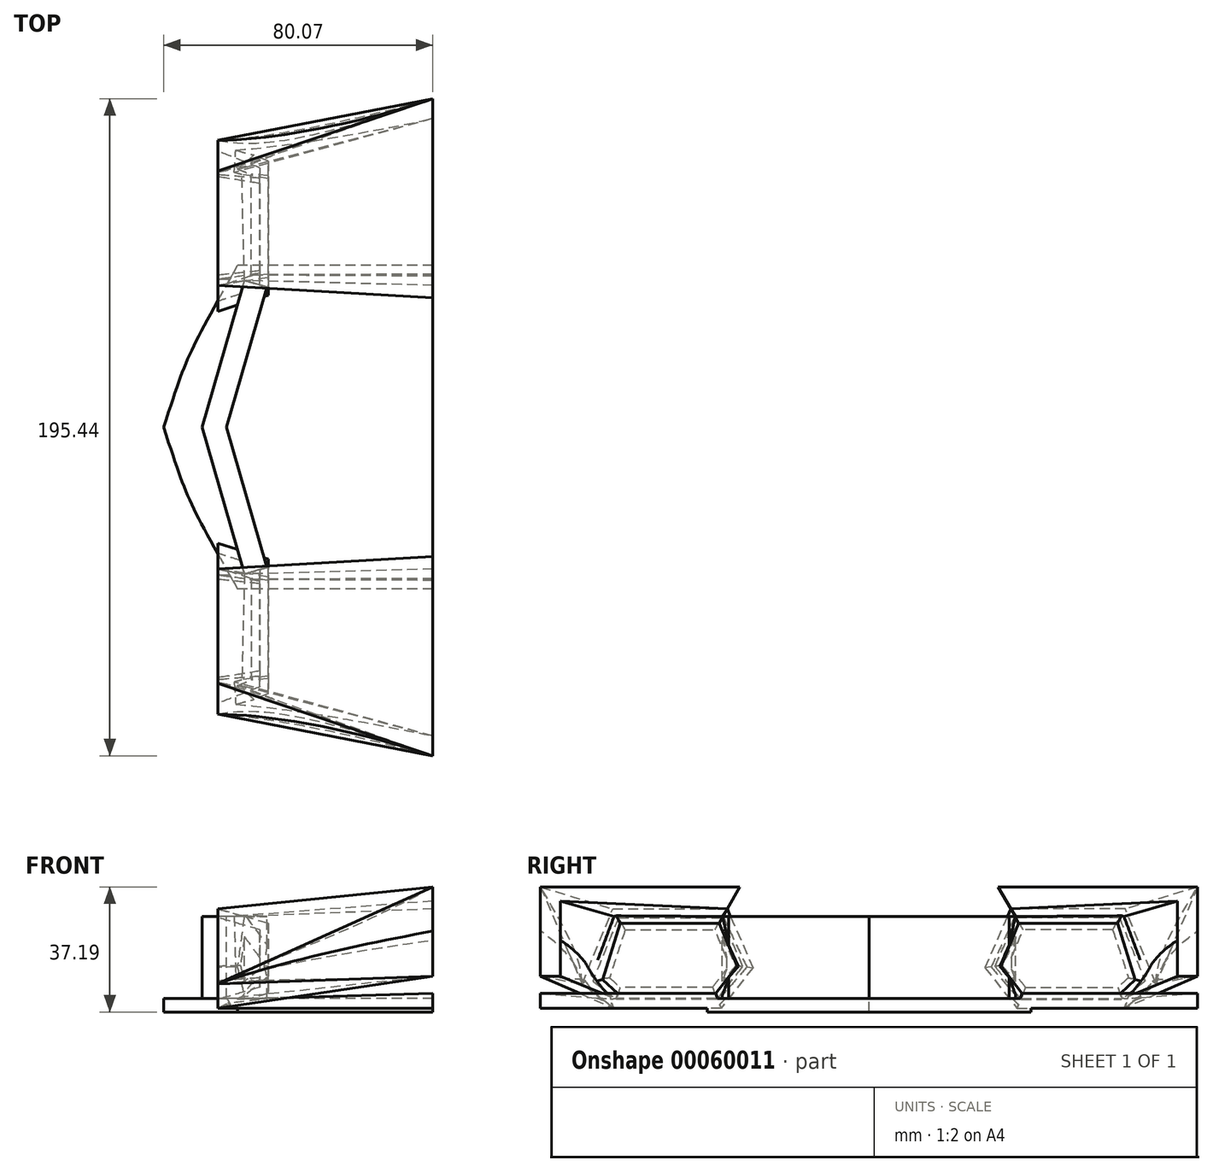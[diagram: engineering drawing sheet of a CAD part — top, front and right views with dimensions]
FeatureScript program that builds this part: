
annotation { "Feature Type Name" : "Feature", "Feature Type Description" : "" }
export const myFeature = defineFeature(function(context is Context, id is Id, definition is map)
    precondition{}
    {
        {
            var Q0;
            Q0=qCreatedBy(makeId("Top.planeOp"),FACE);
            var sketch = newSketch(context, id + "F0", { "sketchPlane" : qUnion([Q0])});
            skPoint(sketch, "E0", {"position": v(-74.63, 89.12) * mm});
            skPoint(sketch, "E1", {"position": v(-74.63, 0) * mm});
            skPoint(sketch, "E2", {"position": v(-156.71, 98.72) * mm});
            skPoint(sketch, "E3", {"position": v(-156.71, 88.06) * mm});
            skSolve(sketch);
        }
        {
            var Q0;
            Q0=qCreatedBy(makeId("Front.planeOp"),FACE);
            var sketch = newSketch(context, id + "F1", { "sketchPlane" : qUnion([Q0])});
            skPoint(sketch, "E4.0", {"position": v(-239, 0) * mm});
            skPoint(sketch, "E5.0", {"position": v(239, 0) * mm});
            skPoint(sketch, "E6", {"position": v(-86.17, 65.26) * mm});
            skSolve(sketch);
        }
        {
            var Q0;
            Q0=qCreatedBy(makeId("Right.planeOp"),FACE);
            cPlane(context, id + "F2", {"entities" : qUnion([Q0]), "cplaneType" : CPlaneType.OFFSET, "offset" : 218.37 * mm, "oppositeDirection" : true, "width" : 150 * mm, "height" : 150 * mm});
        }
        {
            var Q0;
            Q0=qCreatedBy(id+"F2.planeOp",FACE);
            var sketch = newSketch(context, id + "F3", { "sketchPlane" : qUnion([Q0])});
            skPoint(sketch, "E7", {"position": v(76.2, 48.85) * mm});
            skLineSegment(sketch, "E8", {"start": v(76.2, 48.85) * mm, "end": v(42.19, 48.85) * mm});
            skLineSegment(sketch, "E9", {"start": v(42.19, 48.85) * mm, "end": v(34.5, 31.38) * mm});
            skLineSegment(sketch, "E10", {"start": v(34.5, 31.38) * mm, "end": v(44, 19.32) * mm});
            skLineSegment(sketch, "E11", {"start": v(44, 19.32) * mm, "end": v(75.98, 19.32) * mm});
            skLineSegment(sketch, "E12", {"start": v(75.98, 19.32) * mm, "end": v(85.33, 26.56) * mm});
            skLineSegment(sketch, "E13", {"start": v(85.33, 26.56) * mm, "end": v(76.2, 48.85) * mm});
            skSolve(sketch);
        }
        {
            var Q0;
            Q0=qCreatedBy(id+"F2.planeOp",FACE);
            cPlane(context, id + "F4", {"entities" : qUnion([Q0]), "cplaneType" : CPlaneType.OFFSET, "offset" : 15 * mm, "width" : 150 * mm, "height" : 150 * mm});
        }
        {
            var Q0;
            Q0=qCreatedBy(id+"F4.planeOp",FACE);
            var sketch = newSketch(context, id + "F5", { "sketchPlane" : qUnion([Q0])});
            skLineSegment(sketch, "E14", {"start": v(73.97, 44.52) * mm, "end": v(44.5, 44.52) * mm});
            skLineSegment(sketch, "E15", {"start": v(44.5, 44.52) * mm, "end": v(39.26, 31.82) * mm});
            skLineSegment(sketch, "E16", {"start": v(39.26, 31.82) * mm, "end": v(45.52, 23.7) * mm});
            skLineSegment(sketch, "E17", {"start": v(45.52, 23.7) * mm, "end": v(74.81, 23.7) * mm});
            skLineSegment(sketch, "E18", {"start": v(74.81, 23.7) * mm, "end": v(79.22, 27.75) * mm});
            skLineSegment(sketch, "E19", {"start": v(79.22, 27.75) * mm, "end": v(73.97, 44.52) * mm});
            skSolve(sketch);
        }
        {
            var Q0;
            Q0=makeQuery(id+"F5.imprint","IMPRINT",FACE,{"disambiguationData":[TD([[makeQuery(id+"F5.imprint","IMPRINT",EDGE,{"derivedFrom":sQuery(id+"F5.wireOp",EDGE,"E14")}),1.0]])]});
            var Q1;
            Q1=makeQuery(id+"F3.imprint","IMPRINT",FACE,{"disambiguationData":[TD([[makeQuery(id+"F3.imprint","IMPRINT",EDGE,{"derivedFrom":sQuery(id+"F3.wireOp",EDGE,"E8")}),1.0]])]});
            loft(context, id + "F6", {"sheetProfilesArray" : [{ "sheetProfileEntities" : qUnion([Q0]) }, { "sheetProfileEntities" : qUnion([Q1]) }]});
        }
        {
            var Q0;
            Q0=makeQuery(id+"F6.opLoft","CAP_FACE",FACE,{"disambiguationData":[OSD([makeQuery(id+"F3.imprint","IMPRINT",FACE,{"disambiguationData":[TD([[makeQuery(id+"F3.imprint","IMPRINT",EDGE,{"derivedFrom":sQuery(id+"F3.wireOp",EDGE,"E8")}),1.0]])]})])],"isStart":true});
            shell(context, id + "F7", {"entities" : qUnion([Q0]), "thickness" : 2.5 * mm});
        }
        {
            var Q0;
            Q0=makeQuery(id+"F6.opLoft","CAP_FACE",FACE,{"disambiguationData":[OSD([makeQuery(id+"F3.imprint","IMPRINT",FACE,{"disambiguationData":[TD([[makeQuery(id+"F3.imprint","IMPRINT",EDGE,{"derivedFrom":sQuery(id+"F3.wireOp",EDGE,"E8")}),1.0]])]})])],"isStart":true});
            var sketch = newSketch(context, id + "F8", { "sketchPlane" : qUnion([Q0])});
            skPoint(sketch, "E20.0", {"position": v(-76.2, 48.85) * mm});
            skPoint(sketch, "E21.0", {"position": v(-74.49, 46.25) * mm});
            skPoint(sketch, "E22.0", {"position": v(-82.13, 27.4) * mm});
            skPoint(sketch, "E23.0", {"position": v(-85.33, 26.56) * mm});
            skLineSegment(sketch, "E24", {"start": v(-85.33, 26.56) * mm, "end": v(-76.2, 48.85) * mm});
            skLineSegment(sketch, "E25", {"start": v(-85.33, 26.56) * mm, "end": v(-82.13, 27.4) * mm});
            skLineSegment(sketch, "E26", {"start": v(-82.13, 27.4) * mm, "end": v(-74.49, 46.25) * mm});
            skLineSegment(sketch, "E27", {"start": v(-74.49, 46.25) * mm, "end": v(-76.2, 48.85) * mm});
            skSolve(sketch);
        }
        {
            var Q0;
            Q0=qCreatedBy(makeId("Front.planeOp"),FACE);
            var sketch = newSketch(context, id + "F9", { "sketchPlane" : qUnion([Q0])});
            skPoint(sketch, "E28", {"position": v(-154.45, 57.19) * mm});
            skSolve(sketch);
        }
        {
            var Q0;
            Q0=qCreatedBy(makeId("Right.planeOp"),FACE);
            var Q1;
            Q1=sQuery(id+"F9.wireOp",VERTEX,"E28");
            cPlane(context, id + "F10", {"entities" : qUnion([Q0, Q1]), "cplaneType" : CPlaneType.PLANE_POINT, "offset" : 150 * mm, "width" : 150 * mm, "height" : 150 * mm});
        }
        {
            var Q0;
            Q0=qCreatedBy(id+"F10.planeOp",FACE);
            var sketch = newSketch(context, id + "F11", { "sketchPlane" : qUnion([Q0])});
            skPoint(sketch, "E29", {"position": v(97.72, 55.38) * mm});
            skLineSegment(sketch, "E30", {"start": v(97.72, 55.38) * mm, "end": v(97.72, 28.82) * mm});
            skLineSegment(sketch, "E31", {"start": v(97.72, 28.82) * mm, "end": v(91.8, 28.82) * mm});
            skLineSegment(sketch, "E32", {"start": v(91.8, 28.82) * mm, "end": v(91.8, 51.17) * mm});
            skLineSegment(sketch, "E33", {"start": v(91.8, 51.17) * mm, "end": v(97.72, 55.38) * mm});
            skSolve(sketch);
        }
        {
            var Q1;
            Q1=makeQuery(id+"F11.imprint","IMPRINT",FACE,{"disambiguationData":[TD([[makeQuery(id+"F11.imprint","IMPRINT",EDGE,{"derivedFrom":sQuery(id+"F11.wireOp",EDGE,"E30")}),-1.0]])]});
            var Q2;
            Q2=makeQuery(id+"F8.imprint","IMPRINT",FACE,{"disambiguationData":[TD([[makeQuery(id+"F8.imprint","IMPRINT",EDGE,{"derivedFrom":sQuery(id+"F8.wireOp",EDGE,"E24")}),1.0]])]});
            loft(context, id + "F12", {"operationType" : NewBodyOperationType.ADD, "sheetProfilesArray" : [{ "sheetProfileEntities" : qUnion([Q1]) }, { "sheetProfileEntities" : qUnion([Q2]) }]});
        }
        {
            var Q0;
            Q0=makeQuery(id+"F6.opLoft","CAP_FACE",FACE,{"disambiguationData":[OSD([makeQuery(id+"F3.imprint","IMPRINT",FACE,{"disambiguationData":[TD([[makeQuery(id+"F3.imprint","IMPRINT",EDGE,{"derivedFrom":sQuery(id+"F3.wireOp",EDGE,"E8")}),1.0]])]})])],"isStart":true});
            var sketch = newSketch(context, id + "F13", { "sketchPlane" : qUnion([Q0])});
            skPoint(sketch, "E34.0", {"position": v(-85.33, 26.56) * mm});
            skPoint(sketch, "E35.0", {"position": v(-82.13, 27.4) * mm});
            skPoint(sketch, "E36.0", {"position": v(-75.1, 21.92) * mm});
            skPoint(sketch, "E37.0", {"position": v(-75.98, 19.32) * mm});
            skLineSegment(sketch, "E38", {"start": v(-85.33, 26.56) * mm, "end": v(-82.13, 27.4) * mm});
            skLineSegment(sketch, "E39", {"start": v(-82.13, 27.4) * mm, "end": v(-75.1, 21.92) * mm});
            skLineSegment(sketch, "E40", {"start": v(-75.1, 21.92) * mm, "end": v(-75.98, 19.32) * mm});
            skLineSegment(sketch, "E41", {"start": v(-75.98, 19.32) * mm, "end": v(-85.33, 26.56) * mm});
            skSolve(sketch);
        }
        {
            var Q0;
            Q0=makeQuery(id+"F12.opLoft","CAP_FACE",FACE,{"disambiguationData":[OSD([makeQuery(id+"F11.imprint","IMPRINT",FACE,{"disambiguationData":[TD([[makeQuery(id+"F11.imprint","IMPRINT",EDGE,{"derivedFrom":sQuery(id+"F11.wireOp",EDGE,"E30")}),-1.0]])]})])],"isStart":true});
            var sketch = newSketch(context, id + "F14", { "sketchPlane" : qUnion([Q0])});
            skFitSpline(sketch, "E42.0", {"points": [v(97.72, 28.82) * mm, v(95.75, 28.82) * mm, v(93.77, 28.82) * mm, v(91.8, 28.82) * mm]});
            skPoint(sketch, "E43.0", {"position": v(75.98, 19.32) * mm});
            skLineSegment(sketch, "E44", {"start": v(91.8, 28.82) * mm, "end": v(91.8, 19.32) * mm});
            skLineSegment(sketch, "E45", {"start": v(91.8, 19.32) * mm, "end": v(97.72, 19.32) * mm});
            skLineSegment(sketch, "E46", {"start": v(97.72, 19.32) * mm, "end": v(97.72, 28.82) * mm});
            skSolve(sketch);
        }
        {
            var Q1;
            Q1=makeQuery(id+"F14.imprint","IMPRINT",FACE,{"disambiguationData":[TD([[makeQuery(id+"F14.imprint","IMPRINT",EDGE,{"derivedFrom":sQuery(id+"F14.wireOp",EDGE,"E42.0")}),-1.0]])]});
            var Q2;
            Q2=makeQuery(id+"F13.imprint","IMPRINT",FACE,{"disambiguationData":[TD([[makeQuery(id+"F13.imprint","IMPRINT",EDGE,{"derivedFrom":sQuery(id+"F13.wireOp",EDGE,"E38")}),-1.0]])]});
            loft(context, id + "F15", {"operationType" : NewBodyOperationType.ADD, "sheetProfilesArray" : [{ "sheetProfileEntities" : qUnion([Q1]) }, { "sheetProfileEntities" : qUnion([Q2]) }]});
        }
        {
            var Q0;
            Q0=makeQuery(id+"F6.opLoft","CAP_FACE",FACE,{"disambiguationData":[OSD([makeQuery(id+"F3.imprint","IMPRINT",FACE,{"disambiguationData":[TD([[makeQuery(id+"F3.imprint","IMPRINT",EDGE,{"derivedFrom":sQuery(id+"F3.wireOp",EDGE,"E8")}),1.0]])]})])],"isStart":true});
            var sketch = newSketch(context, id + "F16", { "sketchPlane" : qUnion([Q0])});
            skPoint(sketch, "E47.0", {"position": v(-76.2, 48.85) * mm});
            skPoint(sketch, "E48.0", {"position": v(-74.49, 46.25) * mm});
            skPoint(sketch, "E49.0", {"position": v(-43.87, 46.25) * mm});
            skPoint(sketch, "E50.0", {"position": v(-42.19, 48.85) * mm});
            skLineSegment(sketch, "E51", {"start": v(-76.2, 48.85) * mm, "end": v(-74.49, 46.25) * mm});
            skLineSegment(sketch, "E52", {"start": v(-76.2, 48.85) * mm, "end": v(-42.19, 48.85) * mm});
            skLineSegment(sketch, "E53", {"start": v(-42.19, 48.85) * mm, "end": v(-43.87, 46.25) * mm});
            skLineSegment(sketch, "E54", {"start": v(-43.87, 46.25) * mm, "end": v(-74.49, 46.25) * mm});
            skSolve(sketch);
        }
        {
            var Q0;
            Q0=makeQuery(id+"F15.boolean.opBoolean","MERGE",FACE,{"derivedFrom":[makeQuery(id+"F12.opLoft","CAP_FACE",FACE,{"disambiguationData":[OSD([makeQuery(id+"F11.imprint","IMPRINT",FACE,{"disambiguationData":[TD([[makeQuery(id+"F11.imprint","IMPRINT",EDGE,{"derivedFrom":sQuery(id+"F11.wireOp",EDGE,"E30")}),-1.0]])]})])],"isStart":true}),makeQuery(id+"F15.opLoft","CAP_FACE",FACE,{"disambiguationData":[OSD([makeQuery(id+"F14.imprint","IMPRINT",FACE,{"disambiguationData":[TD([[makeQuery(id+"F14.imprint","IMPRINT",EDGE,{"derivedFrom":sQuery(id+"F14.wireOp",EDGE,"E42.0")}),-1.0]])]})])],"isStart":true})]});
            var sketch = newSketch(context, id + "F17", { "sketchPlane" : qUnion([Q0])});
            skPoint(sketch, "E55.0", {"position": v(97.72, 55.38) * mm});
            skPoint(sketch, "E56.0", {"position": v(42.19, 48.85) * mm});
            skLineSegment(sketch, "E57", {"start": v(97.72, 55.38) * mm, "end": v(38.45, 55.38) * mm});
            skFitSpline(sketch, "E58.0", {"points": [v(91.8, 51.17) * mm, v(93.77, 52.57) * mm, v(95.75, 53.97) * mm, v(97.72, 55.38) * mm]});
            skLineSegment(sketch, "E59", {"start": v(38.45, 55.38) * mm, "end": v(42.19, 48.85) * mm});
            skLineSegment(sketch, "E60", {"start": v(42.19, 48.85) * mm, "end": v(91.8, 51.17) * mm});
            skSolve(sketch);
        }
        {
            var Q1;
            Q1=makeQuery(id+"F17.imprint","IMPRINT",FACE,{"disambiguationData":[TD([[makeQuery(id+"F17.imprint","IMPRINT",EDGE,{"derivedFrom":sQuery(id+"F17.wireOp",EDGE,"E57")}),1.0]])]});
            var Q2;
            Q2=makeQuery(id+"F16.imprint","IMPRINT",FACE,{"disambiguationData":[TD([[makeQuery(id+"F16.imprint","IMPRINT",EDGE,{"derivedFrom":sQuery(id+"F16.wireOp",EDGE,"E51")}),1.0]])]});
            loft(context, id + "F18", {"operationType" : NewBodyOperationType.ADD, "sheetProfilesArray" : [{ "sheetProfileEntities" : qUnion([Q1]) }, { "sheetProfileEntities" : qUnion([Q2]) }]});
        }
        {
            var Q0;
            Q0=makeQuery(id+"F6.opLoft","CAP_FACE",FACE,{"disambiguationData":[OSD([makeQuery(id+"F3.imprint","IMPRINT",FACE,{"disambiguationData":[TD([[makeQuery(id+"F3.imprint","IMPRINT",EDGE,{"derivedFrom":sQuery(id+"F3.wireOp",EDGE,"E8")}),1.0]])]})])],"isStart":true});
            var sketch = newSketch(context, id + "F19", { "sketchPlane" : qUnion([Q0])});
            skPoint(sketch, "E61.0", {"position": v(-75.98, 19.32) * mm});
            skPoint(sketch, "E62.0", {"position": v(-75.1, 21.92) * mm});
            skPoint(sketch, "E63.0", {"position": v(-45.24, 21.92) * mm});
            skPoint(sketch, "E64.0", {"position": v(-44, 19.32) * mm});
            skLineSegment(sketch, "E65", {"start": v(-75.98, 19.32) * mm, "end": v(-44, 19.32) * mm});
            skLineSegment(sketch, "E66", {"start": v(-44, 19.32) * mm, "end": v(-45.24, 21.92) * mm});
            skLineSegment(sketch, "E67", {"start": v(-45.24, 21.92) * mm, "end": v(-75.1, 21.92) * mm});
            skLineSegment(sketch, "E68", {"start": v(-75.1, 21.92) * mm, "end": v(-75.98, 19.32) * mm});
            skSolve(sketch);
        }
        {
            var Q0;
            Q0=makeQuery(id+"F18.boolean.opBoolean","MERGE",FACE,{"derivedFrom":[makeQuery(id+"F15.boolean.opBoolean","MERGE",FACE,{"derivedFrom":[makeQuery(id+"F12.opLoft","CAP_FACE",FACE,{"disambiguationData":[OSD([makeQuery(id+"F11.imprint","IMPRINT",FACE,{"disambiguationData":[TD([[makeQuery(id+"F11.imprint","IMPRINT",EDGE,{"derivedFrom":sQuery(id+"F11.wireOp",EDGE,"E30")}),-1.0]])]})])],"isStart":true}),makeQuery(id+"F15.opLoft","CAP_FACE",FACE,{"disambiguationData":[OSD([makeQuery(id+"F14.imprint","IMPRINT",FACE,{"disambiguationData":[TD([[makeQuery(id+"F14.imprint","IMPRINT",EDGE,{"derivedFrom":sQuery(id+"F14.wireOp",EDGE,"E42.0")}),-1.0]])]})])],"isStart":true})]}),makeQuery(id+"F18.opLoft","CAP_FACE",FACE,{"disambiguationData":[OSD([makeQuery(id+"F17.imprint","IMPRINT",FACE,{"disambiguationData":[TD([[makeQuery(id+"F17.imprint","IMPRINT",EDGE,{"derivedFrom":sQuery(id+"F17.wireOp",EDGE,"E57")}),1.0]])]})])],"isStart":true})]});
            cPlane(context, id + "F20", {"entities" : qUnion([Q0]), "cplaneType" : CPlaneType.OFFSET, "offset" : 0 * mm, "width" : 150 * mm, "height" : 150 * mm});
        }
        {
            var Q0;
            Q0=qCreatedBy(id+"F20.planeOp",FACE);
            var sketch = newSketch(context, id + "F21", { "sketchPlane" : qUnion([Q0])});
            skPoint(sketch, "E69.0", {"position": v(97.72, 19.32) * mm});
            skPoint(sketch, "E70.0", {"position": v(45.52, 23.7) * mm});
            skPoint(sketch, "E71.0", {"position": v(44, 19.32) * mm});
            skLineSegment(sketch, "E72", {"start": v(44, 19.32) * mm, "end": v(97.72, 19.32) * mm});
            skLineSegment(sketch, "E73", {"start": v(45.52, 23.7) * mm, "end": v(44, 19.32) * mm});
            skLineSegment(sketch, "E74", {"start": v(45.52, 23.7) * mm, "end": v(97.72, 23.7) * mm});
            skLineSegment(sketch, "E75", {"start": v(97.72, 23.7) * mm, "end": v(97.72, 19.32) * mm});
            skSolve(sketch);
        }
        {
            var Q1;
            Q1=makeQuery(id+"F21.imprint","IMPRINT",FACE,{"disambiguationData":[TD([[makeQuery(id+"F21.imprint","IMPRINT",EDGE,{"derivedFrom":sQuery(id+"F21.wireOp",EDGE,"E72")}),1.0]])]});
            var Q2;
            Q2=makeQuery(id+"F19.imprint","IMPRINT",FACE,{"disambiguationData":[TD([[makeQuery(id+"F19.imprint","IMPRINT",EDGE,{"derivedFrom":sQuery(id+"F19.wireOp",EDGE,"E65")}),1.0]])]});
            loft(context, id + "F22", {"operationType" : NewBodyOperationType.ADD, "sheetProfilesArray" : [{ "sheetProfileEntities" : qUnion([Q1]) }, { "sheetProfileEntities" : qUnion([Q2]) }]});
        }
        {
            var Q0;
            Q0=qCreatedBy(makeId("Top.planeOp"),FACE);
            var Q1;
            {var subQ0=sQuery(id+"F21.wireOp",EDGE,"E74");var subQ1=sQuery(id+"F21.wireOp",EDGE,"E73");var subQ2=sQuery(id+"F19.wireOp",EDGE,"E67");var subQ3=sQuery(id+"F19.wireOp",EDGE,"E66");var subQ4=sQuery(id+"F3.wireOp",EDGE,"E12");var subQ5=sQuery(id+"F3.wireOp",EDGE,"E11");var subQ6=sQuery(id+"F3.wireOp",EDGE,"E10");var subQ7=sQuery(id+"F3.wireOp",EDGE,"E9");Q1=makeQuery(id+"F22.boolean.opBoolean","INTERSECT",VERTEX,{"derivedFrom":[makeQuery(id+"F6.opLoft","SWEPT_FACE",FACE,{"disambiguationData":[OSD([subQ6,subQ5,subQ4,sQuery(id+"F5.wireOp",EDGE,"E16"),sQuery(id+"F5.wireOp",EDGE,"E17"),sQuery(id+"F5.wireOp",EDGE,"E18")])]}),makeQuery(id+"F22.opLoft","SWEPT_FACE",FACE,{"disambiguationData":[OSD([subQ7,subQ6,subQ5,sQuery(id+"F19.wireOp",EDGE,"E65"),subQ3,subQ2,sQuery(id+"F21.wireOp",EDGE,"E72"),subQ1,subQ0])]}),makeQuery(id+"F22.opLoft","SWEPT_FACE",FACE,{"disambiguationData":[OSD([subQ7,subQ6,subQ5,subQ4,sQuery(id+"F3.wireOp",EDGE,"E13"),subQ3,subQ2,sQuery(id+"F19.wireOp",EDGE,"E68"),subQ1,subQ0,sQuery(id+"F21.wireOp",EDGE,"E75")])]})]});}
            cPlane(context, id + "F23", {"entities" : qUnion([Q0, Q1]), "cplaneType" : CPlaneType.PLANE_POINT, "offset" : 150 * mm, "width" : 150 * mm, "height" : 150 * mm});
        }
        {
            var Q0;
            Q0=qCreatedBy(id+"F23.planeOp",FACE);
            var sketch = newSketch(context, id + "F24", { "sketchPlane" : qUnion([Q0])});
            skLineSegment(sketch, "E76", {"start": v(-154.45, 0) * mm, "end": v(-234.52, 0) * mm});
            skLineSegment(sketch, "E77", {"start": v(-154.45, 0) * mm, "end": v(-154.45, 48.1) * mm});
            skLineSegment(sketch, "E78", {"start": v(-154.45, 48.1) * mm, "end": v(-212.5, 48.1) * mm});
            skFitSpline(sketch, "E79", {"points": [v(-234.52, 0) * mm, v(-212.5, 48.1) * mm], "startDerivative": vector(21.4, 65.5) * mm, "endDerivative": vector(44.68, 78.83) * mm});
            skSolve(sketch);
        }
        {
            var Q0;
            Q0=makeQuery(id+"F24.imprint","IMPRINT",FACE,{"disambiguationData":[TD([[makeQuery(id+"F24.imprint","IMPRINT",EDGE,{"derivedFrom":sQuery(id+"F24.wireOp",EDGE,"E76")}),-1.0]])]});
            extrude(context, id + "F25", {"entities" : qUnion([Q0]), "operationType" : NewBodyOperationType.ADD, "oppositeDirection" : true, "depth" : 4 * mm});
        }
        {
            var Q0;
            Q0=qCreatedBy(id+"F23.planeOp",FACE);
            var Q1;
            {var subQ0=sQuery(id+"F17.wireOp",EDGE,"E60");var subQ1=sQuery(id+"F17.wireOp",EDGE,"E59");var subQ2=sQuery(id+"F16.wireOp",EDGE,"E54");var subQ3=sQuery(id+"F16.wireOp",EDGE,"E53");var subQ4=sQuery(id+"F3.wireOp",EDGE,"E13");var subQ5=sQuery(id+"F3.wireOp",EDGE,"E10");var subQ6=sQuery(id+"F3.wireOp",EDGE,"E9");var subQ7=sQuery(id+"F3.wireOp",EDGE,"E8");Q1=makeQuery(id+"F18.boolean.opBoolean","INTERSECT",VERTEX,{"derivedFrom":[makeQuery(id+"F6.opLoft","SWEPT_FACE",FACE,{"disambiguationData":[OSD([subQ7,subQ6,subQ4,sQuery(id+"F5.wireOp",EDGE,"E14"),sQuery(id+"F5.wireOp",EDGE,"E15"),sQuery(id+"F5.wireOp",EDGE,"E19")])]}),makeQuery(id+"F18.opLoft","SWEPT_FACE",FACE,{"disambiguationData":[OSD([subQ7,subQ6,subQ5,sQuery(id+"F16.wireOp",EDGE,"E52"),subQ3,subQ2,sQuery(id+"F17.wireOp",EDGE,"E57"),subQ1,subQ0])]}),makeQuery(id+"F18.opLoft","SWEPT_FACE",FACE,{"disambiguationData":[OSD([subQ7,subQ6,subQ5,sQuery(id+"F3.wireOp",EDGE,"E12"),subQ4,sQuery(id+"F11.wireOp",EDGE,"E31"),sQuery(id+"F11.wireOp",EDGE,"E32"),sQuery(id+"F11.wireOp",EDGE,"E33"),sQuery(id+"F16.wireOp",EDGE,"E51"),subQ3,subQ2,sQuery(id+"F17.wireOp",EDGE,"E58.0"),subQ1,subQ0])]})]});}
            cPlane(context, id + "F26", {"entities" : qUnion([Q0, Q1]), "cplaneType" : CPlaneType.PLANE_POINT, "offset" : 150 * mm, "width" : 150 * mm, "height" : 150 * mm});
        }
        {
            var Q0;
            Q0=qCreatedBy(id+"F26.planeOp",FACE);
            var sketch = newSketch(context, id + "F27", { "sketchPlane" : qUnion([Q0])});
            skPoint(sketch, "E80.0", {"position": v(-210.48, 43.66) * mm});
            skLineSegment(sketch, "E81", {"start": v(-210.48, 43.66) * mm, "end": v(-223.12, 0) * mm});
            skLineSegment(sketch, "E82", {"start": v(-210.48, 43.66) * mm, "end": v(-203.8, 41.72) * mm});
            skLineSegment(sketch, "E83", {"start": v(-203.8, 41.72) * mm, "end": v(-215.88, 0) * mm});
            skLineSegment(sketch, "E84", {"start": v(-215.88, 0) * mm, "end": v(-223.12, 0) * mm});
            skSolve(sketch);
        }
        {
            var Q0;
            Q0=makeQuery(id+"F27.imprint","IMPRINT",FACE,{"disambiguationData":[TD([[makeQuery(id+"F27.imprint","IMPRINT",EDGE,{"derivedFrom":sQuery(id+"F27.wireOp",EDGE,"E81")}),1.0]])]});
            extrude(context, id + "F28", {"entities" : qUnion([Q0]), "operationType" : NewBodyOperationType.ADD, "oppositeDirection" : true, "depth" : 25 * mm});
        }
        {
            var Q0;
            Q0=makeQuery(id+"F6.opLoft","SWEPT_BODY",BODY,{"disambiguationData":[OSD([makeQuery(id+"F3.imprint","IMPRINT",FACE,{"disambiguationData":[TD([[makeQuery(id+"F3.imprint","IMPRINT",EDGE,{"derivedFrom":sQuery(id+"F3.wireOp",EDGE,"E8")}),1.0]])]}),makeQuery(id+"F5.imprint","IMPRINT",FACE,{"disambiguationData":[TD([[makeQuery(id+"F5.imprint","IMPRINT",EDGE,{"derivedFrom":sQuery(id+"F5.wireOp",EDGE,"E14")}),1.0]])]})])]});
            var Q1;
            Q1=qCreatedBy(makeId("Front.planeOp"),FACE);
            mirror(context, id + "F29", {"operationType" : NewBodyOperationType.ADD, "entities" : qUnion([Q0]), "mirrorPlane" : qUnion([Q1])});
        }
    });
